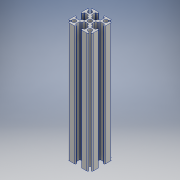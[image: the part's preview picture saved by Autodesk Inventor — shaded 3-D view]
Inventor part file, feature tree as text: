
AUTODESK INVENTOR PART (.ipt)
format: ipt  version: 2018.3 (Build 223284000, 284)  size: 350,720 bytes
history: native  units: mm
features: plane x1, extrude x1, sketch x1, projected_geometry x1, fillet x1
ambient origin geometry x8: Origin, YZ Plane, XZ Plane, XY Plane, X Axis, Y Axis, Z Axis, Center Point
bodies: Solid1 (feature_tree)
feature tree (5):
  plane  "Work Plane1"
  extrude  "Extrusion2"  [1 undecoded]
  sketch  "Sketch3"  dims[d2=925.0mm d3=0.0mm]
  projected_geometry  "Projected Loop3"
  fillet  "Fillet6"  [1 undecoded]
note: 2 required parameter values undecoded (feature->parameter linkage not recoverable at this tier; creation-order binding heuristic only, values carry confidence <= 0.55)
